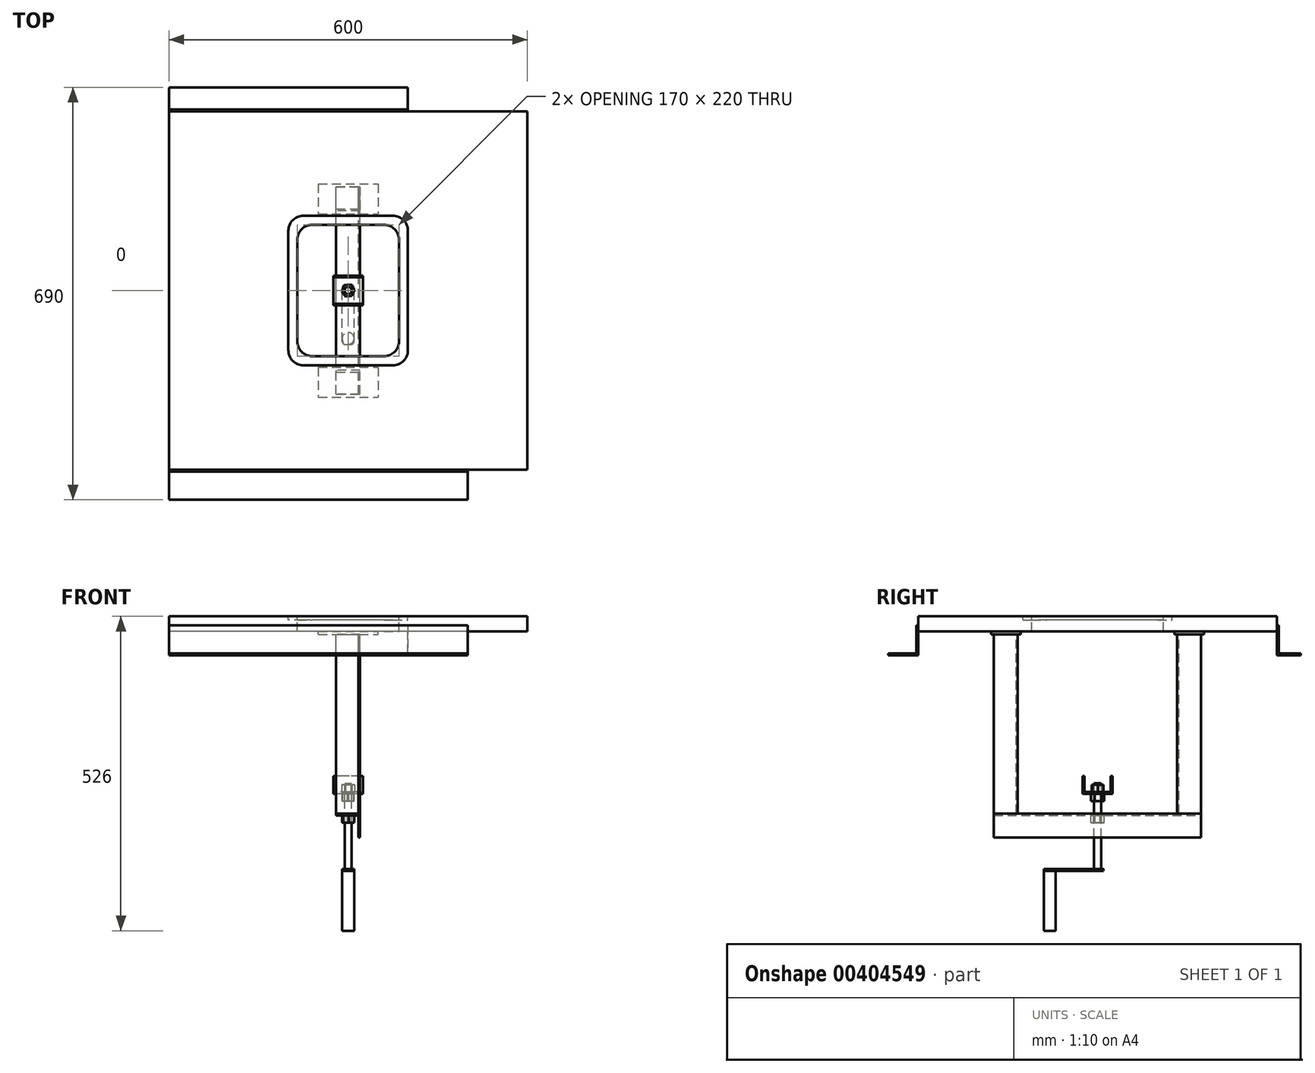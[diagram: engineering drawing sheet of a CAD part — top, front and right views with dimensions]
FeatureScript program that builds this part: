
annotation { "Feature Type Name" : "Feature", "Feature Type Description" : "" }
export const myFeature = defineFeature(function(context is Context, id is Id, definition is map)
    precondition{}
    {
        {
            var Q0;
            Q0=qCreatedBy(makeId("Top.planeOp"),FACE);
            var sketch = newSketch(context, id + "F0", { "sketchPlane" : qUnion([Q0])});
            skLineSegment(sketch, "E0.bottom", {"start": v(300, -300) * mm, "end": v(-300, -300) * mm});
            skLineSegment(sketch, "E0.top", {"start": v(300, 300) * mm, "end": v(-300, 300) * mm});
            skLineSegment(sketch, "E0.left", {"start": v(300, -300) * mm, "end": v(300, 300) * mm});
            skLineSegment(sketch, "E0.right", {"start": v(-300, -300) * mm, "end": v(-300, 300) * mm});
            skPoint(sketch, "E0.middle", {"position": v(0, 0) * mm});
            skSolve(sketch);
        }
        {
            var Q0;
            Q0 = qSketchRegion(id + "F0", true);
            extrude(context, id + "F1", {"entities" : qUnion([Q0]), "oppositeDirection" : true, "depth" : 25 * mm});
        }
        {
            var Q0;
            Q0=makeQuery(id+"F1.opExtrude","SWEPT_FACE",FACE,{"disambiguationData":[OSD([sQuery(id+"F0.wireOp",EDGE,"E0.right")])]});
            var sketch = newSketch(context, id + "F2", { "sketchPlane" : qUnion([Q0])});
            skLineSegment(sketch, "E1", {"start": v(300, -15) * mm, "end": v(300, -65) * mm});
            skLineSegment(sketch, "E2", {"start": v(300, -65) * mm, "end": v(350, -65) * mm});
            skLineSegment(sketch, "E3", {"start": v(350, -65) * mm, "end": v(350, -62) * mm});
            skLineSegment(sketch, "E4", {"start": v(350, -62) * mm, "end": v(303, -62) * mm});
            skLineSegment(sketch, "E5", {"start": v(303, -62) * mm, "end": v(303, -15) * mm});
            skLineSegment(sketch, "E6", {"start": v(303, -15) * mm, "end": v(300, -15) * mm});
            skSolve(sketch);
        }
        {
            var Q0;
            Q0 = qSketchRegion(id + "F2", true);
            extrude(context, id + "F3", {"entities" : qUnion([Q0]), "oppositeDirection" : true, "depth" : 500 * mm});
        }
        {
            var Q0;
            Q0=makeQuery(id+"F1.opExtrude","SWEPT_FACE",FACE,{"disambiguationData":[OSD([sQuery(id+"F0.wireOp",EDGE,"E0.right")])]});
            var sketch = newSketch(context, id + "F4", { "sketchPlane" : qUnion([Q0])});
            skLineSegment(sketch, "E7", {"start": v(-300, -15) * mm, "end": v(-300, -65) * mm});
            skLineSegment(sketch, "E8", {"start": v(-300, -65) * mm, "end": v(-340, -65) * mm});
            skLineSegment(sketch, "E9", {"start": v(-340, -65) * mm, "end": v(-340, -62) * mm});
            skLineSegment(sketch, "E10", {"start": v(-340, -62) * mm, "end": v(-303, -62) * mm});
            skLineSegment(sketch, "E11", {"start": v(-303, -62) * mm, "end": v(-303, -15) * mm});
            skLineSegment(sketch, "E12", {"start": v(-303, -15) * mm, "end": v(-300, -15) * mm});
            skSolve(sketch);
        }
        {
            var Q0;
            Q0 = qSketchRegion(id + "F4", true);
            extrude(context, id + "F5", {"entities" : qUnion([Q0]), "oppositeDirection" : true, "depth" : 400 * mm});
        }
        {
            var Q0;
            Q0=makeQuery(id+"F1.opExtrude","CAP_FACE",FACE,{"disambiguationData":[OSD([sQuery(id+"F0.wireOp",EDGE,"E0.bottom"),sQuery(id+"F0.wireOp",EDGE,"E0.top"),sQuery(id+"F0.wireOp",EDGE,"E0.left"),sQuery(id+"F0.wireOp",EDGE,"E0.right")])],"isStart":true});
            var sketch = newSketch(context, id + "F6", { "sketchPlane" : qUnion([Q0])});
            skLineSegment(sketch, "E13.bottom", {"start": v(75, 125) * mm, "end": v(-75, 125) * mm});
            skLineSegment(sketch, "E13.top", {"start": v(75, -125) * mm, "end": v(-75, -125) * mm});
            skLineSegment(sketch, "E13.left", {"start": v(100, 100) * mm, "end": v(100, -100) * mm});
            skLineSegment(sketch, "E13.right", {"start": v(-100, 100) * mm, "end": v(-100, -100) * mm});
            skPoint(sketch, "E13.middle", {"position": v(0, 0) * mm});
            skPoint(sketch, "E14.visualSharp", {"position": v(-100, -125) * mm});
            skArc(sketch, "E14.filletArc", {"start": v(-100, -100) * mm, "mid": v(-92.68, -117.68) * mm, "end": v(-75, -125) * mm});
            skPoint(sketch, "E15.visualSharp", {"position": v(100, -125) * mm});
            skArc(sketch, "E15.filletArc", {"start": v(75, -125) * mm, "mid": v(92.68, -117.68) * mm, "end": v(100, -100) * mm});
            skPoint(sketch, "E16.visualSharp", {"position": v(100, 125) * mm});
            skArc(sketch, "E16.filletArc", {"start": v(100, 100) * mm, "mid": v(92.68, 117.68) * mm, "end": v(75, 125) * mm});
            skPoint(sketch, "E17.visualSharp", {"position": v(-100, 125) * mm});
            skArc(sketch, "E17.filletArc", {"start": v(-75, 125) * mm, "mid": v(-92.68, 117.68) * mm, "end": v(-100, 100) * mm});
            skCircle(sketch, "E18", {"center": v(0, 0) * mm, "radius": 50 * mm});
            skSolve(sketch);
        }
        {
            var Q0;
            Q0 = qSketchRegion(id + "F6", true);
            extrude(context, id + "F7", {"entities" : qUnion([Q0]), "oppositeDirection" : true, "depth" : 6 * mm});
        }
        {
            var Q0;
            Q0=makeQuery(id+"F7.opExtrude","SWEPT_BODY",BODY,{"disambiguationData":[OSD([sQuery(id+"F6.wireOp",EDGE,"E13.bottom"),sQuery(id+"F6.wireOp",EDGE,"E13.top"),sQuery(id+"F6.wireOp",EDGE,"E13.left"),sQuery(id+"F6.wireOp",EDGE,"E13.right"),sQuery(id+"F6.wireOp",EDGE,"E14.filletArc"),sQuery(id+"F6.wireOp",EDGE,"E15.filletArc"),sQuery(id+"F6.wireOp",EDGE,"E16.filletArc"),sQuery(id+"F6.wireOp",EDGE,"E17.filletArc")])]});
            var Q1;
            Q1=makeQuery(id+"F1.opExtrude","SWEPT_BODY",BODY,{"disambiguationData":[OSD([sQuery(id+"F0.wireOp",EDGE,"E0.bottom"),sQuery(id+"F0.wireOp",EDGE,"E0.top"),sQuery(id+"F0.wireOp",EDGE,"E0.left"),sQuery(id+"F0.wireOp",EDGE,"E0.right")])]});
            booleanBodies(context, id + "F8", {"operationType" : BooleanOperationType.SUBTRACTION, "tools" : qUnion([Q0]), "targets" : qUnion([Q1]), "keepTools" : true});
        }
        {
            var Q0;
            {var subQ0=sQuery(id+"F0.wireOp",EDGE,"E0.bottom");var subQ1=sQuery(id+"F0.wireOp",EDGE,"E0.right");var subQ2=sQuery(id+"F0.wireOp",EDGE,"E0.top");var subQ3=sQuery(id+"F0.wireOp",EDGE,"E0.left");Q0=makeQuery(id+"F8.opBoolean","SPLIT",FACE,{"disambiguationData":[TD([makeQuery(id+"F1.opExtrude","SWEPT_FACE",FACE,{"disambiguationData":[OSD([subQ0])]})])],"derivedFrom":makeQuery(id+"F1.opExtrude","CAP_FACE",FACE,{"disambiguationData":[OSD([subQ0,subQ2,subQ3,subQ1])],"isStart":true})});}
            var sketch = newSketch(context, id + "F9", { "sketchPlane" : qUnion([Q0])});
            skLineSegment(sketch, "E19.bottom", {"start": v(60, 110) * mm, "end": v(-60, 110) * mm});
            skLineSegment(sketch, "E19.top", {"start": v(60, -110) * mm, "end": v(-60, -110) * mm});
            skLineSegment(sketch, "E19.left", {"start": v(85, 85) * mm, "end": v(85, -85) * mm});
            skLineSegment(sketch, "E19.right", {"start": v(-85, 85) * mm, "end": v(-85, -85) * mm});
            skPoint(sketch, "E19.middle", {"position": v(0, 0) * mm});
            skPoint(sketch, "E20.visualSharp", {"position": v(-85, -110) * mm});
            skArc(sketch, "E20.filletArc", {"start": v(-85, -85) * mm, "mid": v(-77.68, -102.68) * mm, "end": v(-60, -110) * mm});
            skPoint(sketch, "E21.visualSharp", {"position": v(85, -110) * mm});
            skArc(sketch, "E21.filletArc", {"start": v(60, -110) * mm, "mid": v(77.68, -102.68) * mm, "end": v(85, -85) * mm});
            skPoint(sketch, "E22.visualSharp", {"position": v(85, 110) * mm});
            skArc(sketch, "E22.filletArc", {"start": v(85, 85) * mm, "mid": v(77.68, 102.68) * mm, "end": v(60, 110) * mm});
            skPoint(sketch, "E23.visualSharp", {"position": v(-85, 110) * mm});
            skArc(sketch, "E23.filletArc", {"start": v(-60, 110) * mm, "mid": v(-77.68, 102.68) * mm, "end": v(-85, 85) * mm});
            skSolve(sketch);
        }
        {
            var Q0;
            Q0 = qSketchRegion(id + "F9", true);
            extrude(context, id + "F10", {"entities" : qUnion([Q0]), "operationType" : NewBodyOperationType.REMOVE, "endBound" : BoundingType.THROUGH_ALL, "oppositeDirection" : true, "depth" : 25 * mm});
        }
        {
            var Q0;
            Q0=makeQuery(id+"F1.opExtrude","CAP_FACE",FACE,{"disambiguationData":[OSD([sQuery(id+"F0.wireOp",EDGE,"E0.bottom"),sQuery(id+"F0.wireOp",EDGE,"E0.top"),sQuery(id+"F0.wireOp",EDGE,"E0.left"),sQuery(id+"F0.wireOp",EDGE,"E0.right")])],"isStart":false});
            var sketch = newSketch(context, id + "F11", { "sketchPlane" : qUnion([Q0])});
            skLineSegment(sketch, "E24.bottom", {"start": v(-50, 128.37) * mm, "end": v(50, 128.37) * mm});
            skLineSegment(sketch, "E24.top", {"start": v(-50, 178.37) * mm, "end": v(50, 178.37) * mm});
            skLineSegment(sketch, "E24.left", {"start": v(-50, 128.37) * mm, "end": v(-50, 178.37) * mm});
            skLineSegment(sketch, "E24.right", {"start": v(50, 128.37) * mm, "end": v(50, 178.37) * mm});
            skPoint(sketch, "E24.middle", {"position": v(0, 153.37) * mm});
            skLineSegment(sketch, "E25.bottom", {"start": v(-50, -178.37) * mm, "end": v(50, -178.37) * mm});
            skLineSegment(sketch, "E25.top", {"start": v(-50, -128.37) * mm, "end": v(50, -128.37) * mm});
            skLineSegment(sketch, "E25.left", {"start": v(-50, -178.37) * mm, "end": v(-50, -128.37) * mm});
            skLineSegment(sketch, "E25.right", {"start": v(50, -178.37) * mm, "end": v(50, -128.37) * mm});
            skPoint(sketch, "E25.middle", {"position": v(0, -153.37) * mm});
            skLineSegment(sketch, "E26", {"start": v(0, 0) * mm, "end": v(154.44, 0) * mm, "construction": true});
            skSolve(sketch);
        }
        {
            var Q0;
            Q0 = qSketchRegion(id + "F11", true);
            extrude(context, id + "F12", {"entities" : qUnion([Q0]), "depth" : 5 * mm});
        }
        {
            var Q0;
            Q0=makeQuery(id+"F12.opExtrude","CAP_FACE",FACE,{"disambiguationData":[OSD([sQuery(id+"F11.wireOp",EDGE,"E24.bottom"),sQuery(id+"F11.wireOp",EDGE,"E24.top"),sQuery(id+"F11.wireOp",EDGE,"E24.left"),sQuery(id+"F11.wireOp",EDGE,"E24.right")])],"isStart":false});
            var sketch = newSketch(context, id + "F13", { "sketchPlane" : qUnion([Q0])});
            skLineSegment(sketch, "E27", {"start": v(20, 173.37) * mm, "end": v(20, 133.37) * mm});
            skLineSegment(sketch, "E28", {"start": v(20, 133.37) * mm, "end": v(-20, 133.37) * mm});
            skLineSegment(sketch, "E29", {"start": v(-20, 133.37) * mm, "end": v(-20, 136.37) * mm});
            skLineSegment(sketch, "E30", {"start": v(-20, 136.37) * mm, "end": v(17, 136.37) * mm});
            skLineSegment(sketch, "E31", {"start": v(17, 136.37) * mm, "end": v(17, 173.37) * mm});
            skLineSegment(sketch, "E32", {"start": v(17, 173.37) * mm, "end": v(20, 173.37) * mm});
            skLineSegment(sketch, "E33", {"start": v(0, 0) * mm, "end": v(0, 195.86) * mm, "construction": true});
            skPoint(sketch, "E33.endSnap0", {"position": v(0, 178.37) * mm});
            skLineSegment(sketch, "E34", {"start": v(50, 153.37) * mm, "end": v(-61.46, 153.37) * mm, "construction": true});
            skSolve(sketch);
        }
        {
            var Q0;
            Q0 = qSketchRegion(id + "F13", true);
            extrude(context, id + "F14", {"entities" : qUnion([Q0]), "depth" : 300 * mm});
        }
        {
            var Q0;
            Q0=makeQuery(id+"F14.opExtrude","SWEPT_BODY",BODY,{"disambiguationData":[OSD([sQuery(id+"F13.wireOp",EDGE,"E27"),sQuery(id+"F13.wireOp",EDGE,"E28"),sQuery(id+"F13.wireOp",EDGE,"E29"),sQuery(id+"F13.wireOp",EDGE,"E30"),sQuery(id+"F13.wireOp",EDGE,"E31"),sQuery(id+"F13.wireOp",EDGE,"E32")])]});
            var Q1;
            Q1=qCreatedBy(makeId("Front.planeOp"),FACE);
            mirror(context, id + "F15", {"entities" : qUnion([Q0]), "mirrorPlane" : qUnion([Q1])});
        }
        {
            var Q0;
            Q0=makeQuery(id+"F14.opExtrude","SWEPT_FACE",FACE,{"disambiguationData":[OSD([sQuery(id+"F13.wireOp",EDGE,"E30")])]});
            var sketch = newSketch(context, id + "F16", { "sketchPlane" : qUnion([Q0])});
            skLineSegment(sketch, "E35", {"start": v(20, -370) * mm, "end": v(20, -330) * mm});
            skLineSegment(sketch, "E36", {"start": v(20, -330) * mm, "end": v(-20, -330) * mm});
            skLineSegment(sketch, "E37", {"start": v(-20, -330) * mm, "end": v(-20, -333) * mm});
            skLineSegment(sketch, "E38", {"start": v(-20, -333) * mm, "end": v(17, -333) * mm});
            skLineSegment(sketch, "E39", {"start": v(17, -333) * mm, "end": v(17, -370) * mm});
            skLineSegment(sketch, "E40", {"start": v(17, -370) * mm, "end": v(20, -370) * mm});
            skSolve(sketch);
        }
        {
            var Q0;
            Q0 = qSketchRegion(id + "F16", true);
            var Q1;
            Q1=makeQuery(id+"F14.opExtrude","SWEPT_FACE",FACE,{"disambiguationData":[OSD([sQuery(id+"F13.wireOp",EDGE,"E32")])]});
            var Q2;
            Q2=makeQuery(id+"F15.opPattern","COPY",FACE,{"derivedFrom":makeQuery(id+"F14.opExtrude","SWEPT_FACE",FACE,{"disambiguationData":[OSD([sQuery(id+"F13.wireOp",EDGE,"E32")])]}),"instanceName":"1"});
            extrude(context, id + "F17", {"entities" : qUnion([Q0]), "endBound" : BoundingType.UP_TO_SURFACE, "endBoundEntityFace" : qUnion([Q1]), "depth" : 25 * mm, "hasSecondDirection" : true, "secondDirectionBound" : BoundingType.UP_TO_SURFACE, "secondDirectionOppositeDirection" : true, "secondDirectionBoundEntityFace" : qUnion([Q2]), "secondDirectionDepth" : 25 * mm});
        }
        {
            var Q0;
            Q0=makeQuery(id+"F17.opExtrude","SWEPT_FACE",FACE,{"disambiguationData":[OSD([sQuery(id+"F16.wireOp",EDGE,"E38")])]});
            var sketch = newSketch(context, id + "F18", { "sketchPlane" : qUnion([Q0])});
            skCircle(sketch, "E41.cCircle", {"center": v(0, 0) * mm, "radius": 9.5 * mm, "construction": true});
            skLineSegment(sketch, "E41.0", {"start": v(-1.4, -10.88) * mm, "end": v(-10.13, -4.22) * mm});
            skLineSegment(sketch, "E41.1", {"start": v(-10.13, -4.22) * mm, "end": v(-8.72, 6.66) * mm});
            skLineSegment(sketch, "E41.2", {"start": v(-8.72, 6.66) * mm, "end": v(1.4, 10.88) * mm});
            skLineSegment(sketch, "E41.3", {"start": v(1.4, 10.88) * mm, "end": v(10.13, 4.22) * mm});
            skLineSegment(sketch, "E41.4", {"start": v(10.13, 4.22) * mm, "end": v(8.72, -6.66) * mm});
            skLineSegment(sketch, "E41.5", {"start": v(8.72, -6.66) * mm, "end": v(-1.4, -10.88) * mm});
            skPoint(sketch, "E41.0.midPoint", {"position": v(-5.77, -7.55) * mm});
            skSolve(sketch);
        }
        {
            var Q0;
            Q0 = qSketchRegion(id + "F18", true);
            extrude(context, id + "F19", {"entities" : qUnion([Q0]), "depth" : 12 * mm});
        }
        {
            var Q0;
            Q0=makeQuery(id+"F19.opExtrude","CAP_FACE",FACE,{"disambiguationData":[OSD([sQuery(id+"F18.wireOp",EDGE,"E41.0"),sQuery(id+"F18.wireOp",EDGE,"E41.1"),sQuery(id+"F18.wireOp",EDGE,"E41.2"),sQuery(id+"F18.wireOp",EDGE,"E41.3"),sQuery(id+"F18.wireOp",EDGE,"E41.4"),sQuery(id+"F18.wireOp",EDGE,"E41.5")])],"isStart":false});
            var sketch = newSketch(context, id + "F20", { "sketchPlane" : qUnion([Q0])});
            skCircle(sketch, "E42", {"center": v(0, 0) * mm, "radius": 6 * mm});
            skSolve(sketch);
        }
        {
            var Q0;
            Q0 = qSketchRegion(id + "F20", true);
            extrude(context, id + "F21", {"entities" : qUnion([Q0]), "depth" : 78 * mm, "hasSecondDirection" : true, "secondDirectionOppositeDirection" : true, "secondDirectionDepth" : 66 * mm});
        }
        {
            var Q0;
            Q0=makeQuery(id+"F21.opExtrude","CAP_FACE",FACE,{"disambiguationData":[OSD([sQuery(id+"F20.wireOp",EDGE,"E42")])],"isStart":false});
            var sketch = newSketch(context, id + "F22", { "sketchPlane" : qUnion([Q0])});
            skLineSegment(sketch, "E43.bottom", {"start": v(-10, 90) * mm, "end": v(10, 90) * mm});
            skLineSegment(sketch, "E43.top", {"start": v(-10, -10) * mm, "end": v(10, -10) * mm});
            skLineSegment(sketch, "E43.left", {"start": v(-10, 90) * mm, "end": v(-10, -10) * mm});
            skLineSegment(sketch, "E43.right", {"start": v(10, 90) * mm, "end": v(10, -10) * mm});
            skPoint(sketch, "E43.middle", {"position": v(0, 40) * mm});
            skSolve(sketch);
        }
        {
            var Q0;
            Q0 = qSketchRegion(id + "F22", true);
            extrude(context, id + "F23", {"entities" : qUnion([Q0]), "depth" : 3 * mm});
        }
        {
            var Q0;
            Q0=makeQuery(id+"F23.opExtrude","SWEPT_EDGE",EDGE,{"disambiguationData":[OSD([sQuery(id+"F22.wireOp",EDGE,"E43.bottom"),sQuery(id+"F22.wireOp",EDGE,"E43.left")])]});
            var Q1;
            Q1=makeQuery(id+"F23.opExtrude","SWEPT_EDGE",EDGE,{"disambiguationData":[OSD([sQuery(id+"F22.wireOp",EDGE,"E43.bottom"),sQuery(id+"F22.wireOp",EDGE,"E43.right")])]});
            var Q2;
            Q2=makeQuery(id+"F23.opExtrude","SWEPT_EDGE",EDGE,{"disambiguationData":[OSD([sQuery(id+"F22.wireOp",EDGE,"E43.top"),sQuery(id+"F22.wireOp",EDGE,"E43.right")])]});
            var Q3;
            Q3=makeQuery(id+"F23.opExtrude","SWEPT_EDGE",EDGE,{"disambiguationData":[OSD([sQuery(id+"F22.wireOp",EDGE,"E43.top"),sQuery(id+"F22.wireOp",EDGE,"E43.left")])]});
            fillet(context, id + "F24", {"entities" : qUnion([Q0, Q1, Q2, Q3]), "radius" : 5 * mm, "tangentPropagation" : true, "allowEdgeOverflow" : false});
        }
        {
            var Q0;
            Q0=makeQuery(id+"F23.opExtrude","CAP_FACE",FACE,{"disambiguationData":[OSD([sQuery(id+"F22.wireOp",EDGE,"E43.bottom"),sQuery(id+"F22.wireOp",EDGE,"E43.top"),sQuery(id+"F22.wireOp",EDGE,"E43.left"),sQuery(id+"F22.wireOp",EDGE,"E43.right")])],"isStart":false});
            var sketch = newSketch(context, id + "F25", { "sketchPlane" : qUnion([Q0])});
            skCircle(sketch, "E44", {"center": v(0, 80) * mm, "radius": 10 * mm});
            skSolve(sketch);
        }
        {
            var Q0;
            Q0 = qSketchRegion(id + "F25", true);
            extrude(context, id + "F26", {"entities" : qUnion([Q0]), "depth" : 100 * mm});
        }
        {
            var Q0;
            Q0=qCreatedBy(makeId("Right.planeOp"),FACE);
            var sketch = newSketch(context, id + "F27", { "sketchPlane" : qUnion([Q0])});
            skLineSegment(sketch, "E45", {"start": v(-25, -267) * mm, "end": v(-25, -297) * mm});
            skLineSegment(sketch, "E46", {"start": v(-25, -297) * mm, "end": v(25, -297) * mm});
            skLineSegment(sketch, "E47", {"start": v(25, -297) * mm, "end": v(25, -267) * mm});
            skLineSegment(sketch, "E48", {"start": v(25, -267) * mm, "end": v(22, -267) * mm});
            skLineSegment(sketch, "E49", {"start": v(22, -267) * mm, "end": v(22, -294) * mm});
            skLineSegment(sketch, "E50", {"start": v(22, -294) * mm, "end": v(-22, -294) * mm});
            skLineSegment(sketch, "E51", {"start": v(-22, -294) * mm, "end": v(-22, -267) * mm});
            skLineSegment(sketch, "E52", {"start": v(-22, -267) * mm, "end": v(-25, -267) * mm});
            skLineSegment(sketch, "E53", {"start": v(0, 0) * mm, "end": v(0, -345.15) * mm, "construction": true});
            skSolve(sketch);
        }
        {
            var Q0;
            Q0 = qSketchRegion(id + "F27", true);
            extrude(context, id + "F28", {"entities" : qUnion([Q0]), "depth" : 50 * mm, "symmetric" : true});
        }
        {
            var Q0;
            Q0=makeQuery(id+"F28.opExtrude","SWEPT_FACE",FACE,{"disambiguationData":[OSD([sQuery(id+"F27.wireOp",EDGE,"E50")])]});
            var sketch = newSketch(context, id + "F29", { "sketchPlane" : qUnion([Q0])});
            skCircle(sketch, "E54.cCircle", {"center": v(0, 0) * mm, "radius": 9.5 * mm, "construction": true});
            skLineSegment(sketch, "E54.0", {"start": v(4.35, 10.07) * mm, "end": v(10.9, 1.26) * mm});
            skLineSegment(sketch, "E54.1", {"start": v(10.9, 1.26) * mm, "end": v(6.54, -8.8) * mm});
            skLineSegment(sketch, "E54.2", {"start": v(6.54, -8.8) * mm, "end": v(-4.35, -10.07) * mm});
            skLineSegment(sketch, "E54.3", {"start": v(-4.35, -10.07) * mm, "end": v(-10.9, -1.26) * mm});
            skLineSegment(sketch, "E54.4", {"start": v(-10.9, -1.26) * mm, "end": v(-6.54, 8.8) * mm});
            skLineSegment(sketch, "E54.5", {"start": v(-6.54, 8.8) * mm, "end": v(4.35, 10.07) * mm});
            skPoint(sketch, "E54.0.midPoint", {"position": v(7.62, 5.67) * mm});
            skCircle(sketch, "E55.0", {"center": v(0, 0) * mm, "radius": 6 * mm});
            skSolve(sketch);
        }
        {
            var Q0;
            Q0 = qSketchRegion(id + "F29", true);
            extrude(context, id + "F30", {"entities" : qUnion([Q0]), "depth" : 12 * mm});
        }
        {
            var Q0;
            Q0=makeQuery(id+"F28.opExtrude","SWEPT_FACE",FACE,{"disambiguationData":[OSD([sQuery(id+"F27.wireOp",EDGE,"E46")])]});
            var sketch = newSketch(context, id + "F31", { "sketchPlane" : qUnion([Q0])});
            skCircle(sketch, "E56.cCircle", {"center": v(0, 0) * mm, "radius": 9.5 * mm, "construction": true});
            skLineSegment(sketch, "E56.0", {"start": v(-1.13, -10.91) * mm, "end": v(-10.01, -4.48) * mm});
            skLineSegment(sketch, "E56.1", {"start": v(-10.01, -4.48) * mm, "end": v(-8.89, 6.43) * mm});
            skLineSegment(sketch, "E56.2", {"start": v(-8.89, 6.43) * mm, "end": v(1.13, 10.91) * mm});
            skLineSegment(sketch, "E56.3", {"start": v(1.13, 10.91) * mm, "end": v(10.01, 4.48) * mm});
            skLineSegment(sketch, "E56.4", {"start": v(10.01, 4.48) * mm, "end": v(8.89, -6.43) * mm});
            skLineSegment(sketch, "E56.5", {"start": v(8.89, -6.43) * mm, "end": v(-1.13, -10.91) * mm});
            skPoint(sketch, "E56.0.midPoint", {"position": v(-5.57, -7.7) * mm});
            skCircle(sketch, "E57.0", {"center": v(0, 0) * mm, "radius": 6 * mm});
            skSolve(sketch);
        }
        {
            var Q0;
            Q0 = qSketchRegion(id + "F31", true);
            extrude(context, id + "F32", {"entities" : qUnion([Q0]), "depth" : 12 * mm});
        }
    });
